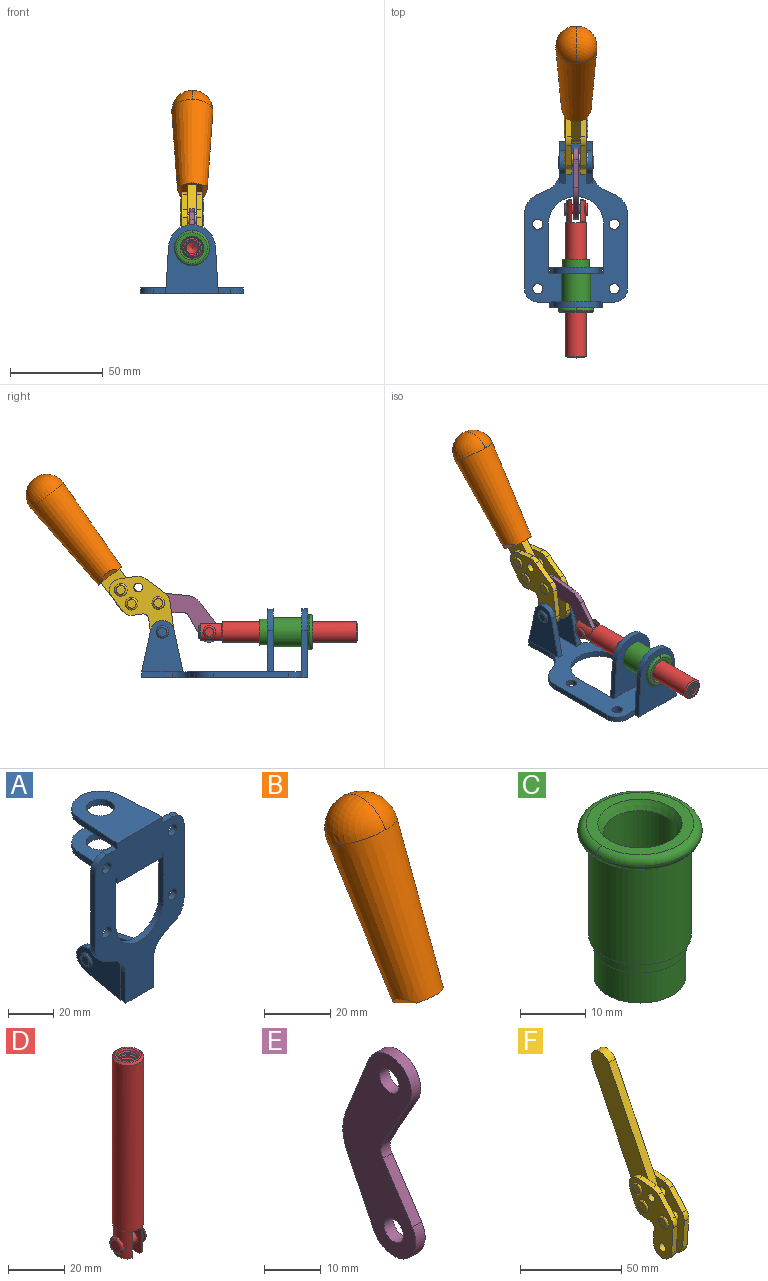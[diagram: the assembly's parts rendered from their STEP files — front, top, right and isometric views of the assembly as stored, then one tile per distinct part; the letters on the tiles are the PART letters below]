
ASSEMBLY  parts=6 mates=6
PART A: 55 faces, bbox 55.7x37.4x89.8 mm
  f0: torus R=2.41mm, axis (-1,0,0), area 15mm2, adj f11,f15,f25
  f1: torus R=2.41mm, axis (-1,0,0), area 15mm2, adj f10,f12,f22
  f2: cylinder r=2.78mm len=5.56mm, axis (0,-1,0), area 54.2mm2, adj f30,f54
  f3: cylinder r=14.99mm len=29.97mm, axis (0,-1,0), area 145.9mm2, adj f30,f49,f53,f54
  f4: cylinder r=2.78mm len=5.56mm, axis (0,-1,0), area 54.2mm2, adj f30,f54
  f5: cylinder r=2.78mm len=5.56mm, axis (0,-1,0), area 54.2mm2, adj f30,f54
  f6: cylinder r=2.78mm len=5.56mm, axis (0,-1,0), area 54.2mm2, adj f30,f54
  f7: cylinder r=6.35mm len=12.7mm, axis (0,0,1), area 123.6mm2, adj f27,f51
  f8: cylinder r=6.35mm len=12.7mm, axis (0,0,-1), area 124.7mm2, adj f21,f35
  f9: cylinder r=2.41mm len=11.18mm, axis (-1,0,0), area 169.4mm2, adj f16,f19
  f10: plane 4.83x4.83mm, normal (1,0,0), area 18.3mm2, adj f1,f12
  f11: plane 4.83x4.83mm, normal (-1,0,0), area 18.3mm2, adj f0,f15
  f12: torus R=2.41mm, axis (-1,0,0), area 15mm2, adj f1,f10,f22
  f13: cylinder r=6.35mm len=12.41mm, axis (1,0,0), area 53.4mm2, adj f18,f19,f22,f23
  f14: cylinder r=6.35mm len=12.41mm, axis (-1,0,0), area 53.4mm2, adj f16,f17,f24,f25
  f15: torus R=2.41mm, axis (-1,0,0), area 15mm2, adj f0,f11,f25
  f16: plane 27.86x22.35mm, normal (1,0,0), area 425.4mm2, adj f9,f14,f17,f24,f30
  f17: plane 22.86x4.97mm, normal (0,0.21,0.98), area 72.5mm2, adj f14,f16,f25,f30
  f18: plane 22.86x4.97mm, normal (0,0.21,0.98), area 72.5mm2, adj f13,f19,f22,f30
  f19: plane 27.86x22.35mm, normal (-1,0,0), area 425.4mm2, adj f9,f13,f18,f23,f30
  f20: cylinder r=12.7mm len=25.35mm, axis (0,0,-1), area 119.8mm2, adj f21,f34,f35,f36
  f21: plane 34.21x28.07mm, normal (0,0,-1), area 702.4mm2, adj f8,f20,f30,f34,f36
  f22: plane 27.96x22.45mm, normal (1,0,0), area 407.2mm2, adj f1,f12,f13,f18,f23,f30,f42,f43
  f23: plane 22.86x4.97mm, normal (0,0.21,-0.98), area 72.5mm2, adj f13,f19,f22,f44
  f24: plane 22.86x4.97mm, normal (0,0.21,-0.98), area 72.5mm2, adj f14,f16,f25,f44
  f25: plane 27.86x22.35mm, normal (-1,0,0), area 407.1mm2, adj f0,f14,f15,f17,f24,f30,f45,f46
  f26: plane 3.1x0.95mm, normal (0,0,-1), area 2.7mm2, adj f30,f49,f50,f54
  f27: plane 34.21x28.07mm, normal (0,0,1), area 702.4mm2, adj f7,f28,f30,f50,f52
  f28: cylinder r=12.7mm len=25.35mm, axis (0,0,1), area 118.8mm2, adj f27,f50,f51,f52
  f29: plane 3.1x0.95mm, normal (0,0,-1), area 2.7mm2, adj f30,f52,f53,f54
  f30: plane 86.54x55.63mm, normal (0,1,0), area 2362.9mm2, adj f2,f3,f4,f5,f6,f16,f17,f18
  f31: plane 40.56x3.1mm, normal (-1,0,0), area 125.7mm2, adj f30,f32,f48,f54
  f32: cylinder r=7.11mm len=7.11mm, axis (0,-1,0), area 34.6mm2, adj f30,f31,f33,f54
  f33: plane 6.67x3.1mm, normal (0,0,1), area 20.4mm2, adj f30,f32,f34,f54
  f34: plane 25.39x3.13mm, normal (-1,0.06,0), area 79.5mm2, adj f20,f21,f33,f35,f54
  f35: plane 37.31x28.45mm, normal (0,0,1), area 789.9mm2, adj f8,f20,f34,f36,f54
  f36: plane 25.39x3.13mm, normal (1,0.06,0), area 79.5mm2, adj f20,f21,f35,f37,f54
  f37: plane 6.67x3.1mm, normal (0,0,1), area 20.4mm2, adj f30,f36,f38,f54
  f38: cylinder r=7.11mm len=7.11mm, axis (0,-1,0), area 34.6mm2, adj f30,f37,f39,f54
  f39: plane 40.56x3.1mm, normal (1,0,0), area 125.7mm2, adj f30,f38,f40,f54
  f40: cylinder r=11.18mm len=10.16mm, axis (0,-1,0), area 39.5mm2, adj f30,f39,f41,f54
  f41: plane 6.09x3.1mm, normal (0.42,0,-0.91), area 20.8mm2, adj f30,f40,f42,f54
  f42: cylinder r=11.18mm len=9.41mm, axis (0,-1,0), area 37.2mm2, adj f22,f30,f41,f43,f54
  f43: plane 16.5x3.1mm, normal (1,0,0), area 51.1mm2, adj f22,f42,f44,f54
  f44: plane 17.37x3.1mm, normal (0,0,-1), area 53.8mm2, adj f23,f24,f30,f43,f45,f54
  f45: plane 16.5x3.1mm, normal (-1,0,0), area 51.1mm2, adj f25,f44,f46,f54
  f46: cylinder r=11.18mm len=9.41mm, axis (0,-1,0), area 37.2mm2, adj f25,f30,f45,f47,f54
  f47: plane 6.09x3.1mm, normal (-0.42,0,-0.91), area 20.8mm2, adj f30,f46,f48,f54
  f48: cylinder r=11.18mm len=10.16mm, axis (0,-1,0), area 39.5mm2, adj f30,f31,f47,f54
  f49: plane 26.54x3.1mm, normal (-1,0,0), area 82.3mm2, adj f3,f26,f30,f54
  f50: plane 25.39x3.1mm, normal (1,0.06,0), area 78.8mm2, adj f26,f27,f28,f51,f54
  f51: plane 37.31x28.45mm, normal (0,0,-1), area 789.9mm2, adj f7,f28,f50,f52,f54
  f52: plane 25.39x3.1mm, normal (-1,0.06,0), area 78.8mm2, adj f27,f28,f29,f51,f54
  f53: plane 26.54x3.1mm, normal (1,0,0), area 82.3mm2, adj f3,f29,f30,f54
  f54: plane 89.66x55.63mm, normal (0,-1,0), area 2678.5mm2, adj f2,f3,f4,f5,f6,f26,f29,f31
PART B: 11 faces, bbox 22.3x42.6x64.5 mm
  f0: sphere r=11.13mm, area 411.4mm2, adj f1,f8
  f1: cone r=11.11mm half-angle=3.3deg, axis (0,0.44,0.9), area 3251.8mm2, adj f0,f7,f8,f9,f10
  f2: cylinder r=6.16mm len=11.7mm, axis (1,0,0), area 89.5mm2, adj f3,f4,f5,f6
  f3: plane 60.23x36.75mm, normal (-1,0,0), area 763.6mm2, adj f2,f4,f6,f10
  f4: plane 51.37x25.05mm, normal (0,0.9,-0.44), area 264.2mm2, adj f2,f3,f5,f10
  f5: plane 60.23x36.75mm, normal (1,0,0), area 763.6mm2, adj f2,f4,f6,f10
  f6: plane 51.37x25.05mm, normal (0,-0.9,0.44), area 264.2mm2, adj f2,f3,f5,f10
  f7: plane 9.95x5.95mm, normal (0.71,-0.31,-0.64), area 25.8mm2, adj f1,f10
  f8: sphere r=11.13mm, area 411.4mm2, adj f0,f1
  f9: plane 9.95x5.95mm, normal (-0.71,-0.31,-0.64), area 25.8mm2, adj f1,f10
  f10: plane 14.27x11.38mm, normal (0,-0.44,-0.9), area 106.7mm2, adj f1,f3,f4,f5,f6,f7,f9
PART C: 15 faces, bbox 20.6x20.6x28.7 mm
  f0: torus R=8.26mm, axis (0,0,1), area 56.8mm2, adj f1,f10,f12
  f1: torus R=8.26mm, axis (0,0,1), area 56.8mm2, adj f0,f6,f13
  f2: cylinder r=5.59mm len=25.91mm, axis (0,0,1), area 909.6mm2, adj f3,f4
  f3: cone r=6.86mm half-angle=45deg, axis (0,0,-1), area 70.2mm2, adj f2,f14
  f4: cone r=6.47mm half-angle=30deg, axis (0,0,1), area 66.7mm2, adj f2,f13
  f5: cylinder r=7.04mm len=14.07mm, axis (0,0,1), area 252.6mm2, adj f11,f14
  f6: torus R=8.26mm, axis (0,0,1), area 56.8mm2, adj f1,f12,f13
  f7: cylinder r=7.16mm len=14.33mm, axis (0,0,1), area 91.5mm2, adj f9,f11
  f8: cylinder r=7.86mm len=18.42mm, axis (0,0,1), area 909.6mm2, adj f9,f10
  f9: plane 15.72x15.72mm, normal (0,0,-1), area 33mm2, adj f7,f8
  f10: plane 16.51x16.51mm, normal (0,0,-1), area 19.9mm2, adj f0,f8,f12
  f11: plane 14.33x14.33mm, normal (0,0,-1), area 5.7mm2, adj f5,f7
  f12: torus R=8.26mm, axis (0,0,1), area 56.8mm2, adj f0,f6,f10
  f13: plane 16.51x16.51mm, normal (0,0,1), area 82.7mm2, adj f1,f4,f6
  f14: plane 14.07x14.07mm, normal (0,0,-1), area 7.8mm2, adj f3,f5
PART D: 48 faces, bbox 12.6x11.1x86.1 mm
  f0: torus R=2.41mm, axis (-1,0,0), area 15mm2, adj f30,f32,f34
  f1: torus R=2.41mm, axis (-1,0,0), area 15mm2, adj f29,f31,f33
  f2: cylinder r=5.54mm len=72.39mm, axis (0,0,1), area 2518.5mm2, adj f3,f4,f42,f43
  f3: cone r=5.54mm half-angle=45deg, axis (0,0,1), area 7.6mm2, adj f2,f5,f41
  f4: cone r=5.54mm half-angle=45deg, axis (0,0,-1), area 34.9mm2, adj f2,f39
  f5: cylinder r=5.08mm len=11.48mm, axis (0,0,1), area 108.3mm2, adj f3,f7,f8,f41
  f6: cylinder r=2.41mm len=4.83mm, axis (-1,0,0), area 71.2mm2, adj f40,f41
  f7: cylinder r=2.41mm len=4.83mm, axis (-1,0,0), area 7.6mm2, adj f5,f34
  f8: cone r=5.08mm half-angle=45deg, axis (0,0,1), area 10.6mm2, adj f5,f37,f41
  f9: cone r=3.98mm half-angle=45deg, axis (0,0,1), area 17.6mm2, adj f27,f39,f45,f46,f47
  f10: cylinder r=2.41mm len=4.83mm, axis (-1,0,0), area 7.6mm2, adj f33,f38
  f11: cylinder r=3.2mm len=6.4mm, axis (0,0,1), area 78.4mm2, adj f12,f28,f44,f45,f47
  f12: cylinder r=3.2mm len=6.4mm, axis (0,0,1), area 10.5mm2, adj f11,f13,f45,f47
  f13: cylinder r=3.2mm len=6.4mm, axis (0,0,1), area 10.5mm2, adj f12,f14,f45,f47
  f14: cylinder r=3.2mm len=6.4mm, axis (0,0,1), area 10.5mm2, adj f13,f15,f45,f47
  f15: cylinder r=3.2mm len=6.4mm, axis (0,0,1), area 10.5mm2, adj f14,f16,f45,f47
  f16: cylinder r=3.2mm len=6.4mm, axis (0,0,1), area 10.5mm2, adj f15,f17,f45,f47
  f17: cylinder r=3.2mm len=6.4mm, axis (0,0,1), area 10.5mm2, adj f16,f18,f45,f47
  f18: cylinder r=3.2mm len=6.4mm, axis (0,0,1), area 10.5mm2, adj f17,f19,f45,f47
  f19: cylinder r=3.2mm len=6.4mm, axis (0,0,1), area 10.5mm2, adj f18,f20,f45,f47
  f20: cylinder r=3.2mm len=6.4mm, axis (0,0,1), area 10.5mm2, adj f19,f21,f45,f47
  f21: cylinder r=3.2mm len=6.4mm, axis (0,0,1), area 10.5mm2, adj f20,f22,f45,f47
  f22: cylinder r=3.2mm len=6.4mm, axis (0,0,1), area 10.5mm2, adj f21,f23,f45,f47
  f23: cylinder r=3.2mm len=6.4mm, axis (0,0,1), area 10.5mm2, adj f22,f24,f45,f47
  f24: cylinder r=3.2mm len=6.4mm, axis (0,0,1), area 10.5mm2, adj f23,f25,f45,f47
  f25: cylinder r=3.2mm len=6.4mm, axis (0,0,1), area 10.5mm2, adj f24,f26,f45,f47
  f26: cylinder r=3.2mm len=6.4mm, axis (0,0,1), area 10.5mm2, adj f25,f27,f45,f47
  f27: cylinder r=3.2mm len=6.4mm, axis (0,0,1), area 7.4mm2, adj f9,f26,f45,f47
  f28: cone r=3.2mm half-angle=60deg, axis (0,0,1), area 37.2mm2, adj f11
  f29: plane 4.83x4.83mm, normal (-1,0,0), area 18.3mm2, adj f1,f31
  f30: plane 4.83x4.83mm, normal (1,0,0), area 18.3mm2, adj f0,f32
  f31: torus R=2.41mm, axis (-1,0,0), area 15mm2, adj f1,f29,f33
  f32: torus R=2.41mm, axis (-1,0,0), area 15mm2, adj f0,f30,f34
  f33: plane 6.83x6.83mm, normal (1,0,0), area 18.3mm2, adj f1,f10,f31
  f34: plane 6.83x6.83mm, normal (-1,0,0), area 18.3mm2, adj f0,f7,f32
  f35: cone r=5.08mm half-angle=45deg, axis (0,0,1), area 10.6mm2, adj f36,f38,f40
  f36: plane 7.25x1.97mm, normal (0,0,-1), area 10mm2, adj f35,f40
  f37: plane 7.25x1.97mm, normal (0,0,-1), area 10mm2, adj f8,f41
  f38: cylinder r=5.08mm len=11.48mm, axis (0,0,1), area 108.3mm2, adj f10,f35,f40,f42
  f39: plane 9.55x9.55mm, normal (0,0,1), area 22mm2, adj f4,f9
  f40: plane 12.76x10.09mm, normal (1,0,0), area 95.7mm2, adj f6,f35,f36,f38,f42,f43
  f41: plane 12.76x10.09mm, normal (-1,0,0), area 95.7mm2, adj f3,f5,f6,f8,f37,f43
  f42: cone r=5.54mm half-angle=45deg, axis (0,0,1), area 7.6mm2, adj f2,f38,f40
  f43: plane 11.07x4.7mm, normal (0,0,-1), area 50.4mm2, adj f2,f40,f41
  f44: plane 0.89x0.62mm, normal (-1,0,0), area 0.3mm2, adj f11,f45,f46,f47
  f45: bspline ~24.8x7.63mm, area 266.6mm2, adj f9,f11,f12,f13,f14,f15,f16,f17
  f46: bspline ~24.87x7.63mm, area 73.6mm2, adj f9,f44,f45,f47
  f47: bspline ~24.98x7.63mm, area 272.5mm2, adj f9,f11,f12,f13,f14,f15,f16,f17
PART E: 12 faces, bbox 2.3x18.2x42.8 mm
  f0: cylinder r=2.4mm len=4.8mm, axis (1,0,0), area 34.9mm2, adj f4,f11
  f1: cylinder r=10.41mm len=8.47mm, axis (1,0,0), area 20.2mm2, adj f4,f9,f10,f11
  f2: cylinder r=3.05mm len=3.16mm, axis (1,0,0), area 7.7mm2, adj f4,f6,f7,f11
  f3: cylinder r=2.4mm len=4.8mm, axis (1,0,0), area 34.9mm2, adj f4,f11
  f4: plane 42.81x18.23mm, normal (-1,0,0), area 414.1mm2, adj f0,f1,f2,f3,f5,f6,f7,f8
  f5: cylinder r=5.54mm len=10.67mm, axis (1,0,0), area 41.8mm2, adj f4,f6,f10,f11
  f6: plane 11.66x6.53mm, normal (0,-0.87,-0.49), area 30.9mm2, adj f2,f4,f5,f11
  f7: plane 11.17x7.33mm, normal (0,-0.84,0.55), area 30.9mm2, adj f2,f4,f8,f11
  f8: cylinder r=5.54mm len=10.51mm, axis (1,0,0), area 41.8mm2, adj f4,f7,f9,f11
  f9: plane 13.67x6.67mm, normal (0,0.9,-0.44), area 35.1mm2, adj f1,f4,f8,f11
  f10: plane 14.1x5.7mm, normal (0,0.93,0.37), area 35.1mm2, adj f1,f4,f5,f11
  f11: plane 42.81x18.23mm, normal (1,0,0), area 414.1mm2, adj f0,f1,f2,f3,f5,f6,f7,f8
PART F: 59 faces, bbox 12.9x60.2x99.6 mm
  f0: torus R=2.39mm, axis (-1,0,0), area 14.9mm2, adj f20,f43,f51
  f1: torus R=2.39mm, axis (-1,0,0), area 14.9mm2, adj f19,f42,f51
  f2: torus R=2.39mm, axis (-1,0,0), area 14.9mm2, adj f18,f35,f51
  f3: torus R=2.39mm, axis (-1,0,0), area 14.9mm2, adj f14,f17,f23
  f4: torus R=2.39mm, axis (-1,0,0), area 14.9mm2, adj f13,f16,f23
  f5: torus R=2.39mm, axis (-1,0,0), area 14.9mm2, adj f12,f15,f23
  f6: cylinder r=2.39mm len=4.78mm, axis (1,0,0), area 46.5mm2, adj f48,f50,f51
  f7: cylinder r=2.39mm len=4.78mm, axis (1,0,0), area 46.5mm2, adj f50,f51
  f8: cylinder r=6.35mm len=12.68mm, axis (1,0,0), area 61.8mm2, adj f38,f39,f50,f51
  f9: cylinder r=2.39mm len=4.78mm, axis (-1,0,0), area 70.5mm2, adj f46,f50
  f10: cylinder r=2.39mm len=4.78mm, axis (-1,0,0), area 46.5mm2, adj f23,f45,f46
  f11: cylinder r=2.39mm len=4.78mm, axis (-1,0,0), area 46.5mm2, adj f23,f46
  f12: plane 4.78x4.78mm, normal (1,0,0), area 17.9mm2, adj f5,f15
  f13: plane 4.78x4.78mm, normal (1,0,0), area 17.9mm2, adj f4,f16
  f14: plane 4.78x4.78mm, normal (1,0,0), area 17.9mm2, adj f3,f17
  f15: torus R=2.39mm, axis (-1,0,0), area 14.9mm2, adj f5,f12,f23
  f16: torus R=2.39mm, axis (-1,0,0), area 14.9mm2, adj f4,f13,f23
  f17: torus R=2.39mm, axis (-1,0,0), area 14.9mm2, adj f3,f14,f23
  f18: plane 4.78x4.78mm, normal (-1,0,0), area 17.9mm2, adj f2,f35
  f19: plane 4.78x4.78mm, normal (-1,0,0), area 17.9mm2, adj f1,f42
  f20: plane 4.78x4.78mm, normal (-1,0,0), area 17.9mm2, adj f0,f43
  f21: plane 2.26x0.2mm, normal (1,0,0), area 0.2mm2, adj f31,f44
  f22: plane 2.26x0.2mm, normal (-1,0,0), area 0.2mm2, adj f41,f44
  f23: plane 39.37x30.77mm, normal (1,0,0), area 565.5mm2, adj f3,f4,f5,f10,f11,f15,f16,f17
  f24: cylinder r=6.1mm len=4.15mm, axis (-1,0,0), area 14.7mm2, adj f23,f25,f32,f46
  f25: plane 10.25x9.01mm, normal (0,-0.75,0.66), area 42.3mm2, adj f23,f24,f26,f46
  f26: cylinder r=6.35mm len=4.64mm, axis (-1,0,0), area 15.6mm2, adj f23,f25,f27,f46
  f27: plane 15.84x3.1mm, normal (0,-1,-0.07), area 49.2mm2, adj f23,f26,f28,f46
  f28: cylinder r=6.35mm len=12.68mm, axis (-1,0,0), area 61.8mm2, adj f23,f27,f29,f46
  f29: plane 8.11x3.1mm, normal (0,1,0.07), area 25.2mm2, adj f23,f28,f30,f46
  f30: cylinder r=3.05mm len=3.25mm, axis (-1,0,0), area 14.8mm2, adj f23,f29,f31,f46
  f31: plane 5.99x3.1mm, normal (0,0.07,-1), area 18.6mm2, adj f21,f23,f30,f44,f46
  f32: plane 9.5x3.1mm, normal (0,-0.07,1), area 29.5mm2, adj f23,f24,f33,f46,f47
  f33: cylinder r=6.1mm len=8.63mm, axis (-1,0,0), area 39.1mm2, adj f23,f32,f34,f47
  f34: plane 8.65x3.96mm, normal (0,0.91,-0.42), area 29.5mm2, adj f23,f33,f44,f47
  f35: torus R=2.39mm, axis (-1,0,0), area 14.9mm2, adj f2,f18,f51
  f36: plane 10.25x9.01mm, normal (0,-0.75,0.66), area 42.3mm2, adj f37,f49,f50,f51
  f37: cylinder r=6.35mm len=4.64mm, axis (1,0,0), area 15.6mm2, adj f36,f38,f50,f51
  f38: plane 15.84x3.1mm, normal (0,-1,-0.07), area 49.2mm2, adj f8,f37,f50,f51
  f39: plane 8.11x3.1mm, normal (0,1,0.07), area 25.2mm2, adj f8,f40,f50,f51
  f40: cylinder r=3.05mm len=3.25mm, axis (1,0,0), area 14.8mm2, adj f39,f41,f50,f51
  f41: plane 5.99x3.1mm, normal (0,0.07,-1), area 18.6mm2, adj f22,f40,f44,f50,f51
  f42: torus R=2.39mm, axis (-1,0,0), area 14.9mm2, adj f1,f19,f51
  f43: torus R=2.39mm, axis (-1,0,0), area 14.9mm2, adj f0,f20,f51
  f44: cylinder r=6.35mm len=12.12mm, axis (-1,0,0), area 128.9mm2, adj f21,f22,f23,f31,f34,f41,f46,f47
  f45: plane 2.65x1.35mm, normal (1,0,0), area 1mm2, adj f10,f55
  f46: plane 39.08x20.42mm, normal (-1,0,0), area 412.5mm2, adj f9,f10,f11,f24,f25,f26,f27,f28
  f47: plane 77.62x39.82mm, normal (1,0,0), area 850mm2, adj f32,f33,f34,f44,f53,f54,f55
  f48: plane 2.65x1.35mm, normal (-1,0,0), area 1mm2, adj f6,f55
  f49: cylinder r=6.1mm len=4.15mm, axis (1,0,0), area 14.7mm2, adj f36,f50,f51,f56
  f50: plane 39.08x20.42mm, normal (1,0,0), area 412.5mm2, adj f6,f7,f8,f9,f36,f37,f38,f39
  f51: plane 39.37x30.77mm, normal (-1,0,0), area 565.5mm2, adj f0,f1,f2,f6,f7,f8,f35,f36
  f52: plane 8.65x3.96mm, normal (0,0.91,-0.42), area 29.5mm2, adj f44,f51,f57,f58
  f53: plane 68.49x33.4mm, normal (0,0.9,-0.44), area 358.1mm2, adj f44,f47,f54,f58
  f54: cylinder r=6.35mm len=12.06mm, axis (1,0,0), area 93.7mm2, adj f47,f53,f55,f58
  f55: plane 68.49x33.4mm, normal (0,-0.9,0.44), area 358.1mm2, adj f44,f45,f46,f47,f48,f50,f54,f58
  f56: plane 9.5x3.1mm, normal (0,-0.07,1), area 29.5mm2, adj f49,f50,f51,f57,f58
  f57: cylinder r=6.1mm len=8.63mm, axis (1,0,0), area 39.1mm2, adj f51,f52,f56,f58
  f58: plane 77.62x39.82mm, normal (-1,0,0), area 850mm2, adj f44,f52,f53,f54,f55,f56,f57
PLACE A rot(axis=(1,0,0),90deg) t=(-0.46,7.95,0.11)mm fixed
PLACE B rot(axis=(-1,0,0),12deg) t=(-0.27,22.63,61.23)mm
PLACE C rot(axis=(0.58,-0.58,0.58),120deg) t=(24.16,7.95,24.72)mm
PLACE D rot(axis=(1,0,0),90deg) t=(-0.46,30.14,0.11)mm
PLACE E rot(axis=(1,0,0),121.7deg) t=(-0.46,40.76,11.9)mm
PLACE F rot(axis=(-1,0,0),12deg) t=(-0.46,22.63,61.23)mm
MATE revolute E.f3 <-> F.f4  axis (1,0,0) through (-0.46,42.25,40.44)mm
MATE fastened B.f2 <-> F.f54  axis (1,0,0) through (-0.27,103.51,100.05)mm
MATE slider D.f2 <-> C.f2  axis (0,-1,0) through (-0.46,-28.64,24.72)mm
MATE fastened C.f2 <-> A.f7  axis (0,1,0) through (-0.46,-38.45,24.72)mm
MATE cylindrical F.f7 <-> A.f0  axis (-1,0,0) through (1.89,40.04,24.72)mm
MATE revolute E.f5 <-> D.f6  axis (1,0,0) through (-0.46,14.66,24.72)mm
